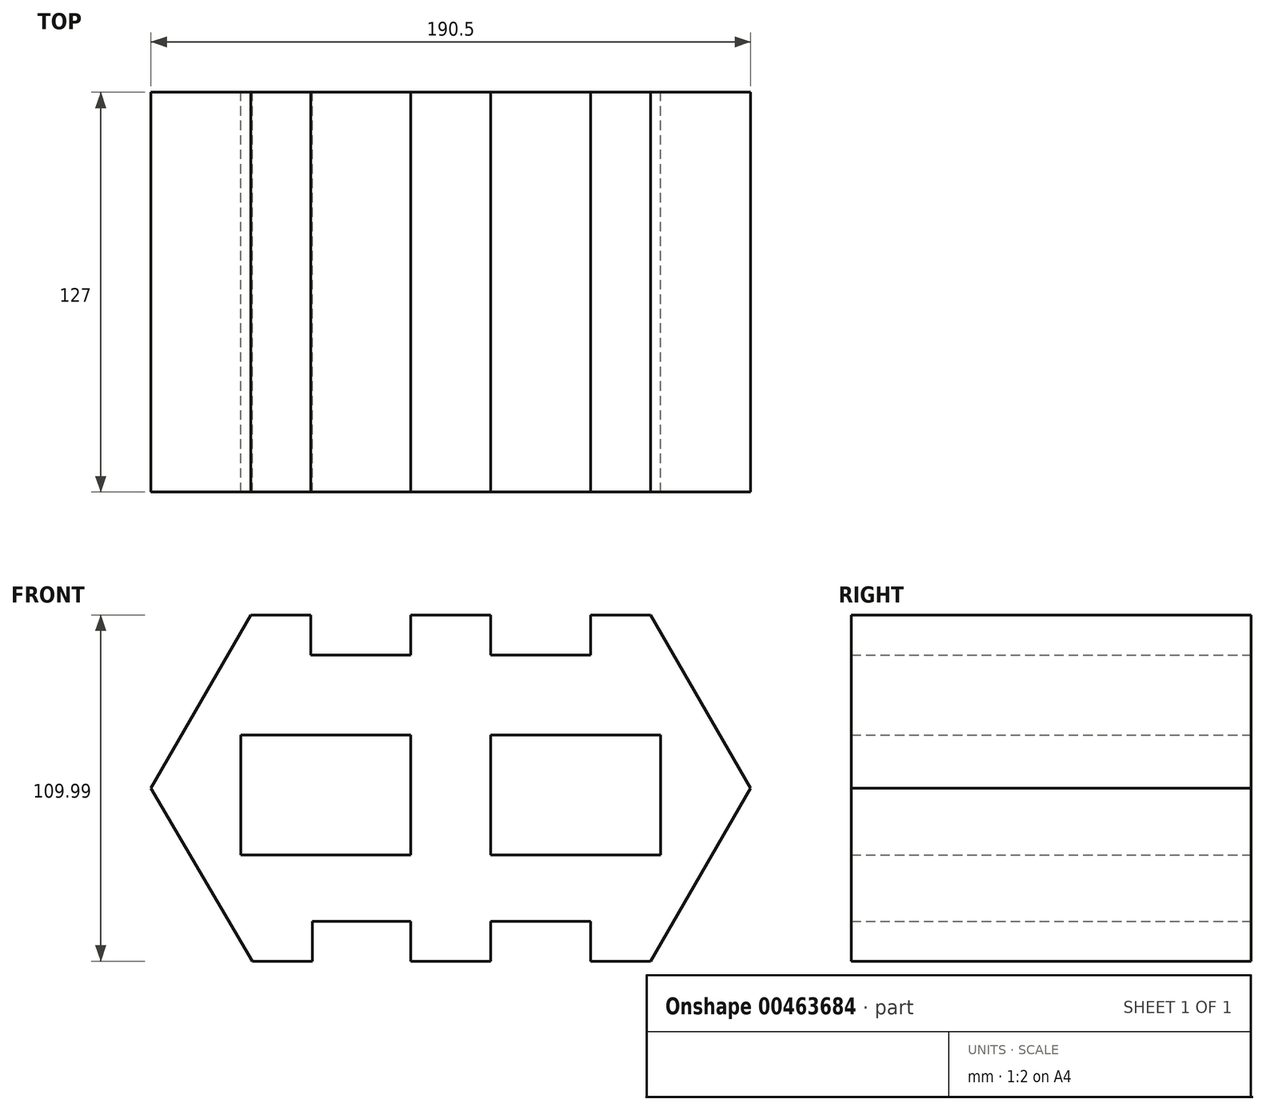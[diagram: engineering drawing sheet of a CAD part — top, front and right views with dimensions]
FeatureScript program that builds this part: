
annotation { "Feature Type Name" : "Feature", "Feature Type Description" : "" }
export const myFeature = defineFeature(function(context is Context, id is Id, definition is map)
    precondition{}
    {
        {
            var Q0;
            Q0=qCreatedBy(makeId("Front.planeOp"),FACE);
            var sketch = newSketch(context, id + "F0", { "sketchPlane" : qUnion([Q0])});
            skLineSegment(sketch, "E0", {"start": v(0, 0) * mm, "end": v(-25.4, 0) * mm});
            skLineSegment(sketch, "E1", {"start": v(-25.4, 0) * mm, "end": v(-25.4, -12.7) * mm});
            skLineSegment(sketch, "E2", {"start": v(-25.4, -12.7) * mm, "end": v(-57.15, -12.7) * mm});
            skLineSegment(sketch, "E3", {"start": v(-57.15, -12.7) * mm, "end": v(-57.15, 0) * mm});
            skLineSegment(sketch, "E4", {"start": v(0, 0) * mm, "end": v(0, -12.7) * mm});
            skLineSegment(sketch, "E5", {"start": v(0, -12.7) * mm, "end": v(31.75, -12.7) * mm});
            skLineSegment(sketch, "E6", {"start": v(31.75, -12.7) * mm, "end": v(31.75, 0) * mm});
            skLineSegment(sketch, "E7", {"start": v(31.75, 0) * mm, "end": v(50.8, 0) * mm});
            skLineSegment(sketch, "E8", {"start": v(-57.15, 0) * mm, "end": v(-76.2, 0) * mm});
            skLineSegment(sketch, "E9", {"start": v(-76.2, 0) * mm, "end": v(-107.95, -55) * mm});
            skLineSegment(sketch, "E10", {"start": v(50.8, 0) * mm, "end": v(82.55, -55) * mm});
            skLineSegment(sketch, "E11.MirrorCS", {"start": v(-75.74, -109.99) * mm, "end": v(-107.95, -55) * mm});
            skLineSegment(sketch, "E12.MirrorCS", {"start": v(-56.69, -97.29) * mm, "end": v(-56.69, -109.99) * mm});
            skLineSegment(sketch, "E13.MirrorCS", {"start": v(-25.4, -97.29) * mm, "end": v(-57.15, -97.29) * mm});
            skLineSegment(sketch, "E14.MirrorCS", {"start": v(-25.4, -109.99) * mm, "end": v(-25.4, -97.29) * mm});
            skPoint(sketch, "E15.start.orphan", {"position": v(-141.9, 0) * mm});
            skPoint(sketch, "E16.endSnap0", {"position": v(-25.4, -6.35) * mm});
            skLineSegment(sketch, "E17", {"start": v(-25.4, -38.1) * mm, "end": v(-79.38, -38.1) * mm});
            skLineSegment(sketch, "E18", {"start": v(-79.38, -38.1) * mm, "end": v(-79.38, -76.2) * mm});
            skLineSegment(sketch, "E19", {"start": v(-79.38, -76.2) * mm, "end": v(-25.4, -76.2) * mm});
            skLineSegment(sketch, "E20", {"start": v(-25.4, -76.2) * mm, "end": v(-25.4, -38.1) * mm});
            skLineSegment(sketch, "E21", {"start": v(0, -38.1) * mm, "end": v(53.98, -38.1) * mm});
            skLineSegment(sketch, "E22", {"start": v(53.98, -38.1) * mm, "end": v(53.98, -76.2) * mm});
            skLineSegment(sketch, "E23", {"start": v(53.98, -76.2) * mm, "end": v(0, -76.2) * mm});
            skLineSegment(sketch, "E24", {"start": v(0, -76.2) * mm, "end": v(0, -38.1) * mm});
            skLineSegment(sketch, "E25", {"start": v(-56.69, -109.99) * mm, "end": v(-75.74, -109.99) * mm});
            skLineSegment(sketch, "E26", {"start": v(0, -97.29) * mm, "end": v(31.75, -97.29) * mm});
            skLineSegment(sketch, "E27", {"start": v(31.75, -97.29) * mm, "end": v(31.75, -109.99) * mm});
            skLineSegment(sketch, "E28", {"start": v(31.75, -109.99) * mm, "end": v(50.8, -109.99) * mm});
            skLineSegment(sketch, "E29", {"start": v(0, -97.29) * mm, "end": v(0, -109.99) * mm});
            skLineSegment(sketch, "E30", {"start": v(0, -109.99) * mm, "end": v(-25.4, -109.99) * mm});
            skLineSegment(sketch, "E31", {"start": v(82.55, -55) * mm, "end": v(50.8, -109.99) * mm});
            skSolve(sketch);
        }
        {
            var Q0;
            Q0 = qSketchRegion(id + "F0", true);
            extrude(context, id + "F1", {"entities" : qUnion([Q0]), "depth" : 127 * mm});
        }
    });
